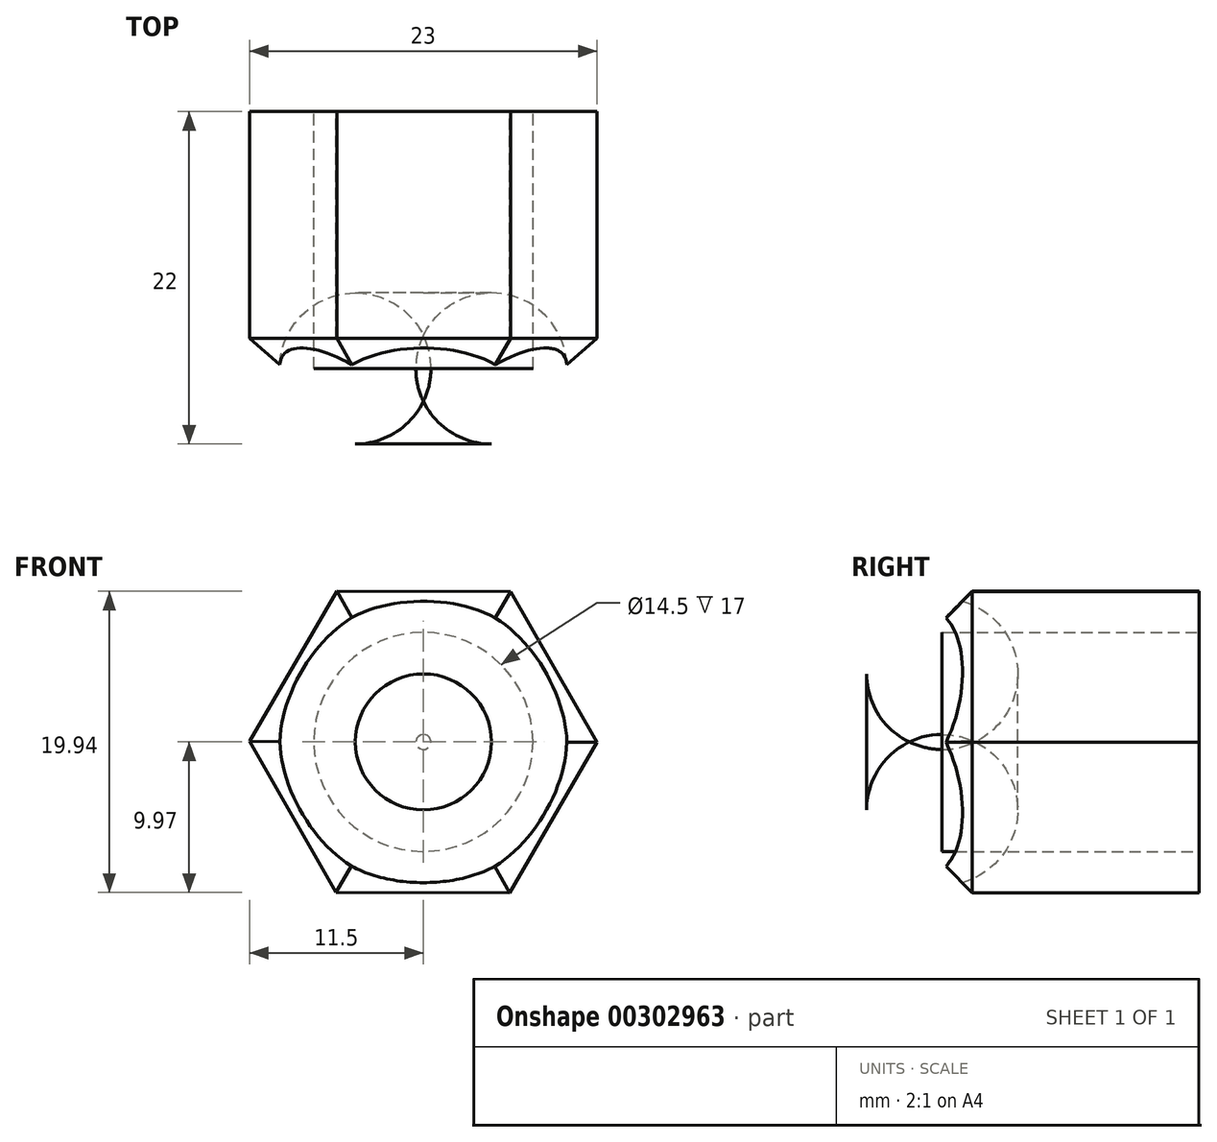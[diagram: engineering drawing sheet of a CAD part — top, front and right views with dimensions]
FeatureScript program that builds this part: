
annotation { "Feature Type Name" : "Feature", "Feature Type Description" : "" }
export const myFeature = defineFeature(function(context is Context, id is Id, definition is map)
    precondition{}
    {
        {
            var Q0;
            Q0=qCreatedBy(makeId("Front.planeOp"),FACE);
            var sketch = newSketch(context, id + "F0", { "sketchPlane" : qUnion([Q0])});
            skCircle(sketch, "E0", {"center": v(0, 0) * mm, "radius": 7.25 * mm});
            skCircle(sketch, "E1.cCircle", {"center": v(0, 0) * mm, "radius": 9.96 * mm, "construction": true});
            skLineSegment(sketch, "E1.0", {"start": v(11.5, -0.03) * mm, "end": v(5.72, -9.97) * mm});
            skLineSegment(sketch, "E1.1", {"start": v(5.72, -9.97) * mm, "end": v(-5.78, -9.94) * mm});
            skLineSegment(sketch, "E1.2", {"start": v(-5.78, -9.94) * mm, "end": v(-11.5, 0.03) * mm});
            skLineSegment(sketch, "E1.3", {"start": v(-11.5, 0.03) * mm, "end": v(-5.72, 9.97) * mm});
            skLineSegment(sketch, "E1.4", {"start": v(-5.72, 9.97) * mm, "end": v(5.78, 9.94) * mm});
            skLineSegment(sketch, "E1.5", {"start": v(5.78, 9.94) * mm, "end": v(11.5, -0.03) * mm});
            skPoint(sketch, "E1.0.midPoint", {"position": v(8.61, -5) * mm});
            skSolve(sketch);
        }
        {
            var Q0;
            Q0 = qSketchRegion(id + "F0", true);
            extrude(context, id + "F1", {"entities" : qUnion([Q0]), "depth" : 17 * mm, "offsetDistance" : 25 * mm});
        }
        {
            var Q0;
            Q0=makeQuery(id+"F1.opExtrude","CAP_FACE",FACE,{"disambiguationData":[OSD([sQuery(id+"F0.wireOp",EDGE,"c27ce71a-ae10-44ab-a06a-f50dae252172.0"),sQuery(id+"F0.wireOp",EDGE,"c27ce71a-ae10-44ab-a06a-f50dae252172.1"),sQuery(id+"F0.wireOp",EDGE,"c27ce71a-ae10-44ab-a06a-f50dae252172.2"),sQuery(id+"F0.wireOp",EDGE,"c27ce71a-ae10-44ab-a06a-f50dae252172.3"),sQuery(id+"F0.wireOp",EDGE,"c27ce71a-ae10-44ab-a06a-f50dae252172.4"),sQuery(id+"F0.wireOp",EDGE,"c27ce71a-ae10-44ab-a06a-f50dae252172.5"),sQuery(id+"F0.wireOp",EDGE,"c27ce71a-ae10-44ab-a06a-f50dae252172.6"),sQuery(id+"F0.wireOp",EDGE,"E0")])],"isStart":false});
            var sketch = newSketch(context, id + "F2", { "sketchPlane" : qUnion([Q0])});
            skCircle(sketch, "E2", {"center": v(0, 0) * mm, "radius": 9.5 * mm});
            skSolve(sketch);
        }
        {
            var Q0;
            Q0 = qSketchRegion(id + "F2", true);
            extrude(context, id + "F3", {"entities" : qUnion([Q0]), "operationType" : NewBodyOperationType.ADD, "depth" : 5 * mm, "offsetDistance" : 25 * mm});
        }
        {
            var Q0;
            Q0=makeQuery(id+"F3.opExtrude","CAP_EDGE",EDGE,{"disambiguationData":[OSD([sQuery(id+"F2.wireOp",EDGE,"E2")])],"isStart":false});
            fillet(context, id + "F4", {"entities" : qUnion([Q0]), "radius" : 5 * mm, "tangentPropagation" : true, "allowEdgeOverflow" : false});
        }
        {
            var Q0;
            Q0=makeQuery(id+"F1.opExtrude","CAP_EDGE",EDGE,{"disambiguationData":[OSD([sQuery(id+"F0.wireOp",EDGE,"E1.2")])],"isStart":false});
            var Q1;
            Q1=makeQuery(id+"F1.opExtrude","CAP_EDGE",EDGE,{"disambiguationData":[OSD([sQuery(id+"F0.wireOp",EDGE,"E1.0")])],"isStart":false});
            var Q2;
            Q2=makeQuery(id+"F1.opExtrude","CAP_EDGE",EDGE,{"disambiguationData":[OSD([sQuery(id+"F0.wireOp",EDGE,"E1.4")])],"isStart":false});
            var Q3;
            Q3=makeQuery(id+"F1.opExtrude","CAP_EDGE",EDGE,{"disambiguationData":[OSD([sQuery(id+"F0.wireOp",EDGE,"E1.5")])],"isStart":false});
            var Q4;
            Q4=makeQuery(id+"F1.opExtrude","CAP_EDGE",EDGE,{"disambiguationData":[OSD([sQuery(id+"F0.wireOp",EDGE,"E1.1")])],"isStart":false});
            var Q5;
            Q5=makeQuery(id+"F1.opExtrude","CAP_EDGE",EDGE,{"disambiguationData":[OSD([sQuery(id+"F0.wireOp",EDGE,"E1.3")])],"isStart":false});
            chamfer(context, id + "F5", {"entities" : qUnion([Q0, Q1, Q2, Q3, Q4, Q5]), "width" : 2 * mm, "tangentPropagation" : true});
        }
    });
